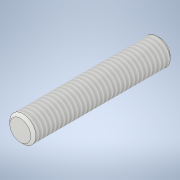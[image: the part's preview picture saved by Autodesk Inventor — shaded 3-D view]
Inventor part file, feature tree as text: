
AUTODESK INVENTOR PART (.ipt)
format: ipt  version: 2022 (Build 260153000, 153)  size: 128,000 bytes
history: native  units: in
note: dims shown in document units (in); Inventor stores cm internally (conversion verified against a paired STEP export)
features: extrude x2, sketch x2, chamfer x1, thread x1
ambient origin geometry x8: Origin, YZ Plane, XZ Plane, XY Plane, X Axis, Y Axis, Z Axis, Center Point
bodies: Body1 (feature_tree)
feature tree (6):
  extrude  "Extrusion1"  Depth=0.6299in
  chamfer  "Chamfer1"  Distance=0.0118in
  thread  "Thread1"  [1 undecoded]
  extrude  "Extrusion2"  Depth=0.0787in TaperAngle=0.0deg
  sketch  "Sketch1"  dims[d0=0.6299in d1=0.0in d2=0.0118in d3=0.0118in d4=17.7165in d5=0.0118in d6=0.0118in d7=17.7165in d8=0.6063in d9=0.0in]
  sketch  "Sketch2"  dims[d10=0.0591in d11=0.0787in d12=0.0in]
note: 1 required parameter value undecoded (feature->parameter linkage not recoverable at this tier; creation-order binding heuristic only, values carry confidence <= 0.55)
